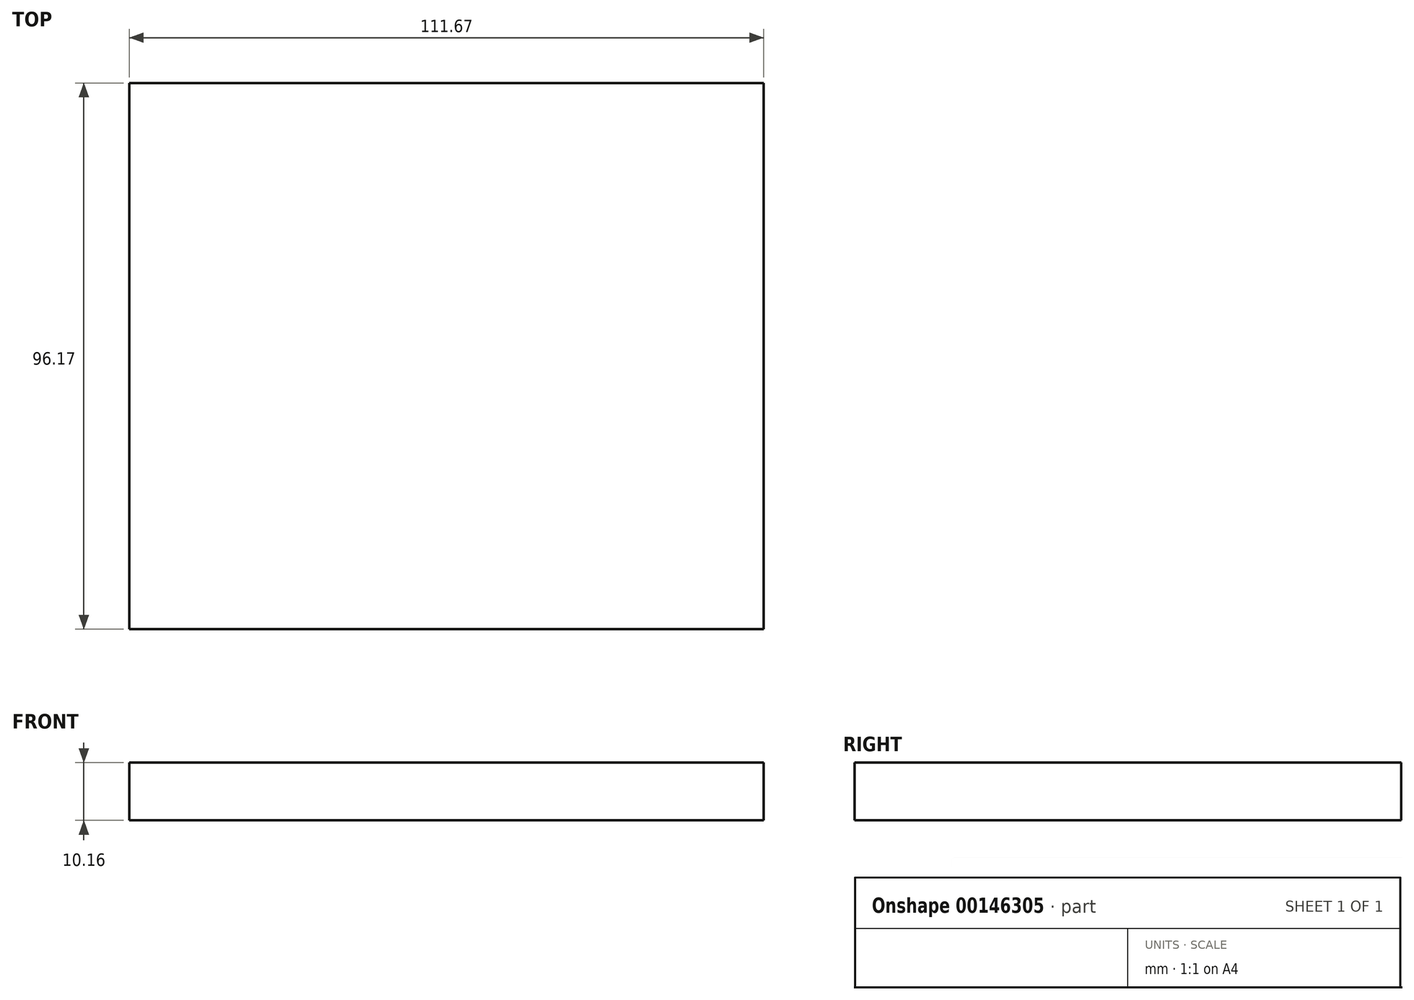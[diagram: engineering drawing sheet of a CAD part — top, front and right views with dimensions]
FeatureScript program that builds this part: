
annotation { "Feature Type Name" : "Feature", "Feature Type Description" : "" }
export const myFeature = defineFeature(function(context is Context, id is Id, definition is map)
    precondition{}
    {
        {
            var Q0;
            Q0=qCreatedBy(makeId("Top.planeOp"),FACE);
            var sketch = newSketch(context, id + "F0", { "sketchPlane" : qUnion([Q0])});
            skLineSegment(sketch, "E0.bottom", {"start": v(-54.23, 42.6) * mm, "end": v(57.44, 42.6) * mm});
            skLineSegment(sketch, "E0.top", {"start": v(-54.23, -53.56) * mm, "end": v(57.44, -53.56) * mm});
            skLineSegment(sketch, "E0.left", {"start": v(-54.23, 42.6) * mm, "end": v(-54.23, -53.56) * mm});
            skLineSegment(sketch, "E0.right", {"start": v(57.44, 42.6) * mm, "end": v(57.44, -53.56) * mm});
            skSolve(sketch);
        }
        {
            var Q0;
            Q0 = qSketchRegion(id + "F0", true);
            extrude(context, id + "F1", {"entities" : qUnion([Q0]), "depth" : 10.16 * mm});
        }
    });
